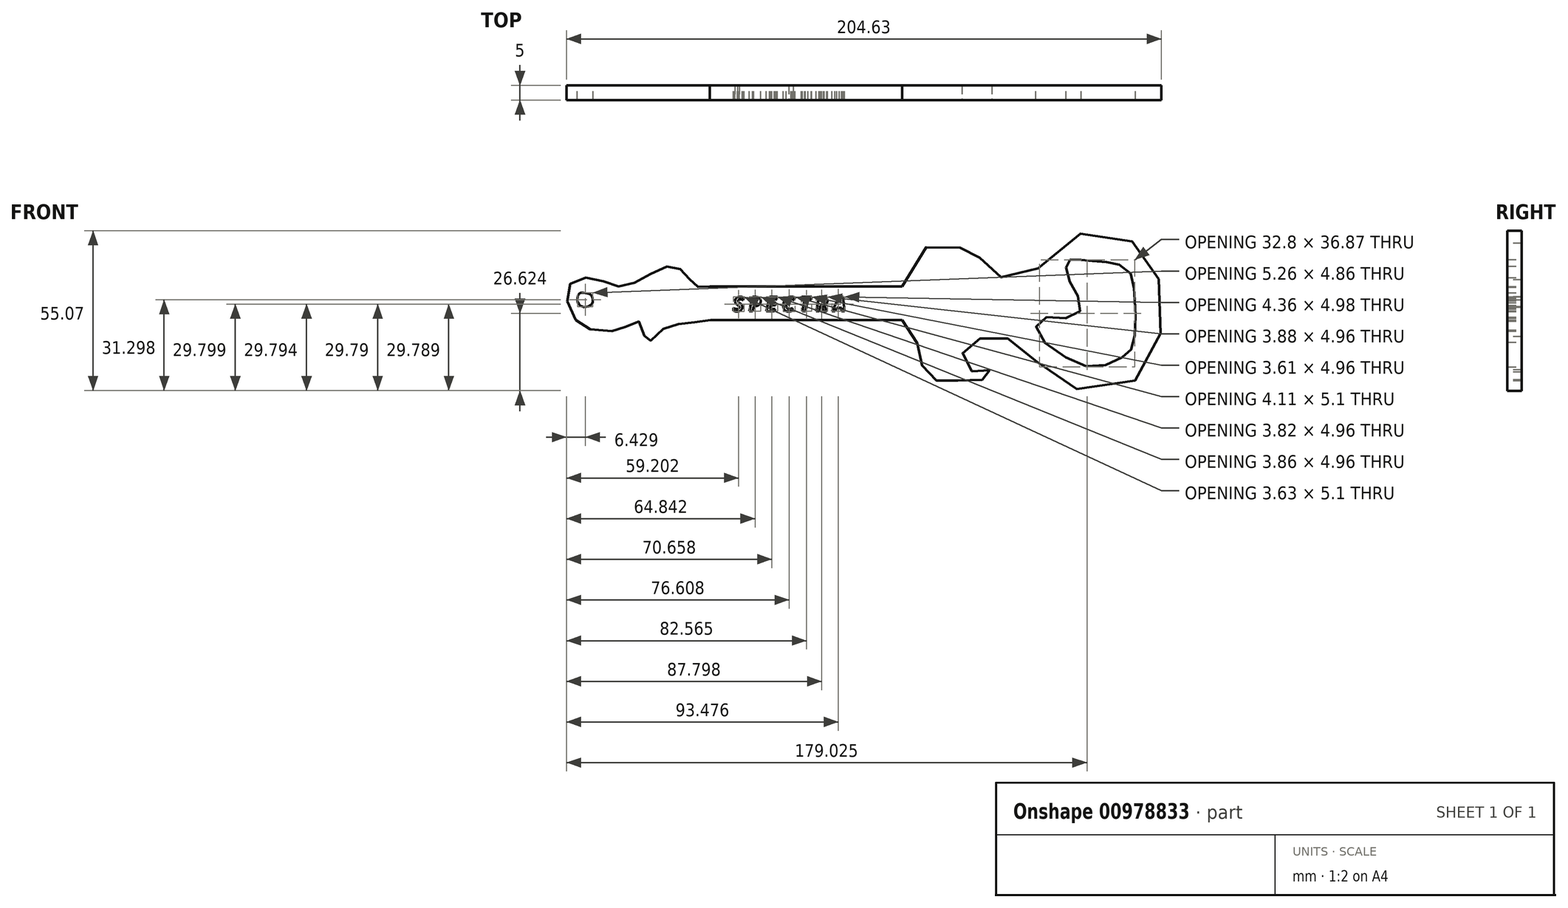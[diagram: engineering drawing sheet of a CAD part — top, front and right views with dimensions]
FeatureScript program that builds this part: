
annotation { "Feature Type Name" : "Feature", "Feature Type Description" : "" }
export const myFeature = defineFeature(function(context is Context, id is Id, definition is map)
    precondition{}
    {
        {
            var Q0;
            Q0=qCreatedBy(makeId("Front.planeOp"),FACE);
            var sketch = newSketch(context, id + "F0", { "sketchPlane" : qUnion([Q0])});
            skLineSegment(sketch, "E0", {"start": v(-54.22, 15.12) * mm, "end": v(12.06, 15.12) * mm});
            skLineSegment(sketch, "E1", {"start": v(-53.94, 3.47) * mm, "end": v(12.06, 3.47) * mm});
            skFitSpline(sketch, "E2", {"points": [v(12.06, 15.12) * mm, v(21.5, 29.26) * mm, v(31.84, 28.42) * mm, v(35.8, 26.8) * mm, v(39.25, 24.55) * mm, v(44.24, 19.28) * mm, v(54.78, 18.44) * mm, v(73.64, 33.42) * mm, v(95.27, 27.32) * mm, v(101.1, 9.57) * mm, v(94.72, -15.4) * mm, v(67.53, -18.72) * mm, v(54.78, -6.8) * mm, v(46.18, -2.36) * mm, v(39.8, -2.63) * mm, v(34.53, -4.3) * mm, v(32.59, -9.3) * mm, v(33.7, -13.17) * mm, v(38.7, -14.28) * mm, v(40.9, -13.73) * mm, v(42.3, -13.73) * mm, v(42.85, -14.56) * mm, v(41.74, -16.5) * mm, v(36.47, -17.06) * mm, v(31.76, -17.33) * mm, v(27.6, -17.33) * mm, v(24, -17.33) * mm, v(20.1, -15.67) * mm, v(18.72, -10.96) * mm, v(17.8, -6.67) * mm, v(16.22, -2.36) * mm, v(12.06, 3.47) * mm], "startDerivative": vector(126.8, 368.32) * mm, "endDerivative": vector(-137.25, 158.9) * mm});
            skFitSpline(sketch, "E3", {"points": [v(-54.22, 15.12) * mm, v(-58.66, 15.12) * mm, v(-61.99, 18.72) * mm, v(-66.98, 22.05) * mm, v(-76.13, 18.44) * mm, v(-85.29, 15.12) * mm, v(-94.16, 17.89) * mm, v(-102.76, 15.12) * mm, v(-99.98, 3.19) * mm, v(-92.5, 0) * mm, v(-89.17, 0) * mm, v(-85.56, 0) * mm, v(-78.35, 2.91) * mm, v(-75.86, -4.02) * mm, v(-70.86, 0) * mm, v(-62.54, 2.36) * mm, v(-53.94, 3.47) * mm], "startDerivative": vector(-98.47, -17.44) * mm, "endDerivative": vector(125.34, 18.38) * mm});
            skFitSpline(sketch, "E4", {"points": [v(73.64, 24.27) * mm, v(76.34, 24) * mm, v(81.61, 23.53) * mm, v(85.43, 22.92) * mm, v(90, 20.39) * mm, v(91.67, 15.04) * mm, v(92, 11.24) * mm, v(92.22, 5.96) * mm, v(91.83, -3.38) * mm, v(90.28, -7.35) * mm, v(86.92, -9.74) * mm, v(78.35, -12.62) * mm, v(67.26, -8.74) * mm, v(58.1, 0) * mm, v(60.6, 4.3) * mm, v(69.48, 4.3) * mm, v(73.64, 7.9) * mm, v(70.86, 14.56) * mm, v(68.74, 19.4) * mm, v(68.64, 23.71) * mm, v(70.39, 24.36) * mm, v(73.64, 24.27) * mm]});
            skText(sketch, "E5", { "text": "S P E C T R A", "fontName": "OpenSans-BoldItalic.ttf"});
            skFitSpline(sketch, "E6", {"points": [v(-96.22, 12.65) * mm, v(-98.74, 12.82) * mm, v(-99.71, 10.59) * mm, v(-98.63, 8.41) * mm, v(-96, 8.18) * mm, v(-94.4, 9.79) * mm, v(-95.02, 12.13) * mm, v(-96.22, 12.65) * mm]});
            const initialGuessF0  = {"E5": [-0.04618, 0.00652, 1, 0, 0.005]};
            skSetInitialGuess(sketch, initialGuessF0);
            skSolve(sketch);
        }
        {
            var Q0;
            Q0=makeQuery(id+"F0.imprint","IMPRINT",FACE,{"disambiguationData":[TD([[makeQuery(id+"F0.imprint","IMPRINT",EDGE,{"derivedFrom":sQuery(id+"F0.wireOp",EDGE,"E0")}),-1.0]])]});
            extrude(context, id + "F1", {"entities" : qUnion([Q0]), "depth" : 5 * mm, "offsetDistance" : 25 * mm});
        }
    });
